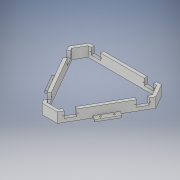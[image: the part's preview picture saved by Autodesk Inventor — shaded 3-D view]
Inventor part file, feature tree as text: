
AUTODESK INVENTOR PART (.ipt)
format: ipt  version: 2018.1 (Build 221171000, 171)  size: 299,008 bytes
history: native  units: mm
features: sketch x7, hole x6, extrude x5
ambient origin geometry x8: Origin, YZ Plane, XZ Plane, XY Plane, X Axis, Y Axis, Z Axis, Center Point
bodies: Body1 (feature_tree)
feature tree (18):
  sketch  "Sketch1"  dims[d0=160.0mm d9=61.283555mm]
  extrude  "Extrusion12"  Depth=61.283555mm
  sketch  "Sketch11"  dims[d10=27.361611mm d11=51.423009mm]
  sketch  "Sketch12"  dims[d12=75.17541mm d15=78.78462mm]
  hole  "Hole8"  [1 undecoded]
  hole  "Hole9"  [1 undecoded]
  sketch  "Sketch13"  dims[d16=13.891854mm d17=13.891854mm]
  hole  "Hole10"  [1 undecoded]
  extrude  "Extrusion13"  Depth=27.361611mm
  extrude  "Extrusion14"  Depth=61.283555mm
  extrude  "Extrusion15"  Depth=5.0mm
  extrude  "Extrusion16"  Depth=5.0mm
  hole  "Hole11"  [1 undecoded]
  hole  "Hole12"  [1 undecoded]
  hole  "Hole13"  [1 undecoded]
  sketch  "Sketch14"  dims[d18=78.78462mm d19=27.361611mm]
  sketch  "Sketch15"  dims[d20=75.17541mm d21=61.283555mm]
  sketch  "Sketch16"  dims[d22=51.423009mm d71=15.55mm d73=15.55mm d74=15.55mm d81=25.0mm d82=120.0deg d83=29.717098mm d86=29.717098mm d87=25.0mm d88=25.736mm d89=7.5mm d93=29.330127mm d210=25.0mm d211=0.0mm d212=8.6mm d213=19.1mm d214=61.284mm d216=2.0mm d217=10.0mm d218=4.0mm d219=2.0mm d220=90.0deg d221=10.0mm d222=20.594885mm d223=8.6mm d224=19.1mm d226=61.284mm d228=61.284mm d229=8.6mm d230=19.1mm d231=2.0mm d232=10.0mm d233=4.0mm d234=2.0mm d235=90.0deg d236=10.0mm d237=20.594885mm d238=8.6mm d239=19.1mm d240=61.284mm d242=19.1mm d243=8.6mm d244=61.284mm d246=8.6mm d247=19.1mm d248=61.284mm d250=2.0mm d251=10.0mm d252=4.0mm d253=2.0mm d254=90.0deg d255=10.0mm d256=20.594885mm d257=2.2mm d258=2.2mm d260=6.3mm d261=10.0mm d262=0.0mm d264=1.0mm d265=10.0mm d266=10.0mm d267=2.2mm d268=2.2mm d269=6.3mm d270=1.0mm d271=1.0mm d272=2.2mm d273=2.2mm d274=6.3mm d275=1.0mm d276=6.3mm d277=2.2mm d278=2.2mm d279=10.0mm d280=0.0mm d281=2.2mm d282=2.2mm d283=1.0mm d284=6.3mm d285=10.0mm d286=10.0mm d287=1.0mm d288=2.2mm d289=2.2mm d290=6.3mm d291=10.0mm d292=0.0mm d293=10.0mm d294=12.5mm d295=65.6mm d296=65.6mm d297=50.027365mm d298=65.6mm d299=65.6mm d300=12.5mm d301=65.6mm d302=65.6mm d303=12.5mm d304=5.0mm d305=0.0mm d306=6.5mm d307=6.5mm d308=12.5mm d309=12.5mm d310=4.5mm d311=6.0mm d312=4.0mm d313=2.0mm d314=90.0deg d315=5.0mm d316=0.0mm d317=6.5mm d318=6.5mm d319=12.5mm d320=12.5mm d321=4.5mm d322=6.0mm d323=4.0mm d324=2.0mm d325=90.0deg d326=5.0mm d327=0.0mm d328=12.5mm d329=12.5mm d330=6.5mm d331=6.5mm d332=4.5mm d333=6.0mm d334=4.0mm d335=2.0mm d336=90.0deg d337=5.0mm d338=0.0mm]
note: 6 required parameter values undecoded (feature->parameter linkage not recoverable at this tier; creation-order binding heuristic only, values carry confidence <= 0.55)
